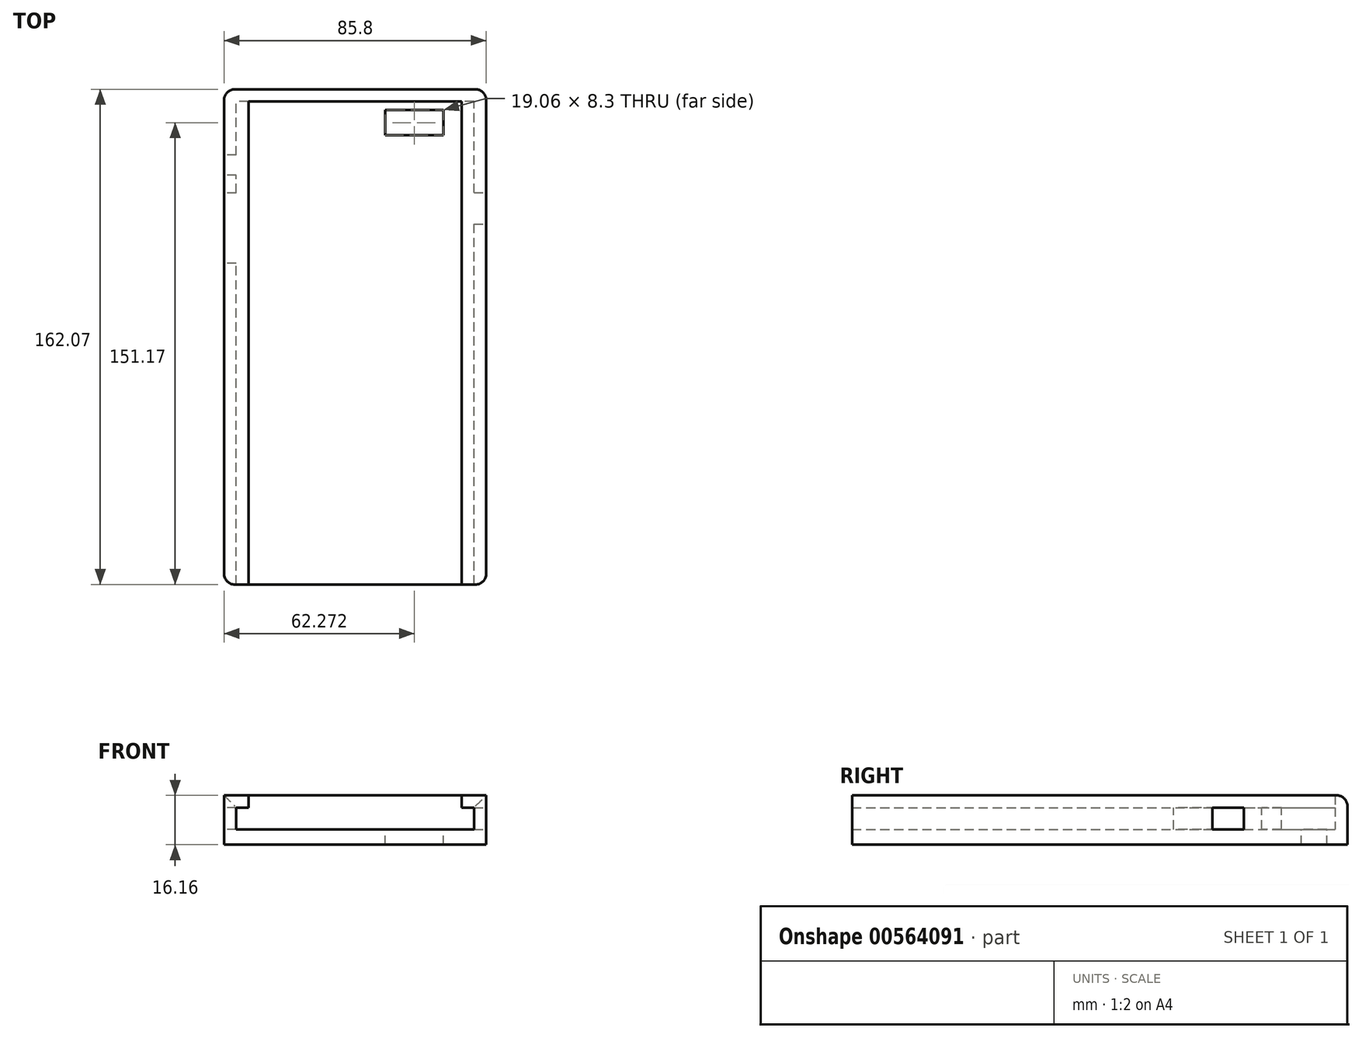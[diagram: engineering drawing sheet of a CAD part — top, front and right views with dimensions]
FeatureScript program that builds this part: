
annotation { "Feature Type Name" : "Feature", "Feature Type Description" : "" }
export const myFeature = defineFeature(function(context is Context, id is Id, definition is map)
    precondition{}
    {
        {
            var Q0;
            Q0=qCreatedBy(makeId("Front.planeOp"),FACE);
            var sketch = newSketch(context, id + "F0", { "sketchPlane" : qUnion([Q0])});
            skLineSegment(sketch, "E0", {"start": v(-41.48, -12.16) * mm, "end": v(44.32, -12.16) * mm});
            skLineSegment(sketch, "E1", {"start": v(44.32, -12.16) * mm, "end": v(44.32, 4) * mm});
            skLineSegment(sketch, "E2", {"start": v(44.32, 4) * mm, "end": v(36.32, 4) * mm});
            skLineSegment(sketch, "E3", {"start": v(36.32, 4) * mm, "end": v(36.32, 0) * mm});
            skLineSegment(sketch, "E4", {"start": v(36.32, 0) * mm, "end": v(40.32, 0) * mm});
            skLineSegment(sketch, "E5", {"start": v(40.32, 0) * mm, "end": v(40.32, -7.1) * mm});
            skLineSegment(sketch, "E6", {"start": v(40.32, -7.1) * mm, "end": v(-37.48, -7.1) * mm});
            skLineSegment(sketch, "E7", {"start": v(-37.48, -7.1) * mm, "end": v(-37.48, 0) * mm});
            skLineSegment(sketch, "E8", {"start": v(-37.48, 0) * mm, "end": v(-33.48, 0) * mm});
            skLineSegment(sketch, "E9", {"start": v(-33.48, 0) * mm, "end": v(-33.48, 4) * mm});
            skLineSegment(sketch, "E10", {"start": v(-33.48, 4) * mm, "end": v(-41.48, 4) * mm});
            skLineSegment(sketch, "E11", {"start": v(-41.48, 4) * mm, "end": v(-41.48, -12.16) * mm});
            skSolve(sketch);
        }
        {
            var Q0;
            Q0 = qSketchRegion(id + "F0", true);
            extrude(context, id + "F1", {"entities" : qUnion([Q0]), "depth" : 158.07 * mm, "offsetDistance" : 25.4 * mm});
        }
        {
            var Q0;
            Q0=makeQuery(id+"F1.opExtrude","CAP_FACE",FACE,{"disambiguationData":[OSD([sQuery(id+"F0.wireOp",EDGE,"E0"),sQuery(id+"F0.wireOp",EDGE,"E1"),sQuery(id+"F0.wireOp",EDGE,"E2"),sQuery(id+"F0.wireOp",EDGE,"E3"),sQuery(id+"F0.wireOp",EDGE,"E4"),sQuery(id+"F0.wireOp",EDGE,"E5"),sQuery(id+"F0.wireOp",EDGE,"E6"),sQuery(id+"F0.wireOp",EDGE,"E7"),sQuery(id+"F0.wireOp",EDGE,"E8"),sQuery(id+"F0.wireOp",EDGE,"E9"),sQuery(id+"F0.wireOp",EDGE,"E10"),sQuery(id+"F0.wireOp",EDGE,"E11")])],"isStart":false});
            var sketch = newSketch(context, id + "F2", { "sketchPlane" : qUnion([Q0])});
            skLineSegment(sketch, "E12.bottom", {"start": v(-41.48, 4) * mm, "end": v(44.32, 4) * mm});
            skLineSegment(sketch, "E12.top", {"start": v(-41.48, -12.16) * mm, "end": v(44.32, -12.16) * mm});
            skLineSegment(sketch, "E12.left", {"start": v(-41.48, 4) * mm, "end": v(-41.48, -12.16) * mm});
            skLineSegment(sketch, "E12.right", {"start": v(44.32, 4) * mm, "end": v(44.32, -12.16) * mm});
            skSolve(sketch);
        }
        {
            var Q0;
            Q0=qCreatedBy(makeId("Front.planeOp"),FACE);
            var sketch = newSketch(context, id + "F3", { "sketchPlane" : qUnion([Q0])});
            skLineSegment(sketch, "E13.bottom", {"start": v(44.32, 4) * mm, "end": v(-41.48, 4) * mm});
            skLineSegment(sketch, "E13.top", {"start": v(44.32, -12.16) * mm, "end": v(-41.48, -12.16) * mm});
            skLineSegment(sketch, "E13.left", {"start": v(44.32, 4) * mm, "end": v(44.32, -12.16) * mm});
            skLineSegment(sketch, "E13.right", {"start": v(-41.48, 4) * mm, "end": v(-41.48, -12.16) * mm});
            skSolve(sketch);
        }
        {
            var Q0;
            Q0 = qSketchRegion(id + "F3", true);
            extrude(context, id + "F4", {"entities" : qUnion([Q0]), "operationType" : NewBodyOperationType.ADD, "oppositeDirection" : true, "depth" : 4 * mm, "offsetDistance" : 25.4 * mm});
        }
        {
            var Q0;
            Q0=makeQuery(id+"F4.opExtrude","CAP_EDGE",EDGE,{"disambiguationData":[OSD([sQuery(id+"F3.wireOp",EDGE,"E13.right")])],"isStart":false});
            var Q1;
            Q1=makeQuery(id+"F4.opExtrude","CAP_EDGE",EDGE,{"disambiguationData":[OSD([sQuery(id+"F3.wireOp",EDGE,"E13.left")])],"isStart":false});
            var Q2;
            Q2=makeQuery(id+"F4.opExtrude","CAP_EDGE",EDGE,{"disambiguationData":[OSD([sQuery(id+"F3.wireOp",EDGE,"E13.bottom")])],"isStart":false});
            var Q3;
            Q3=makeQuery(id+"F1.opExtrude","CAP_EDGE",EDGE,{"disambiguationData":[OSD([sQuery(id+"F0.wireOp",EDGE,"E1")])],"isStart":false});
            var Q4;
            Q4=makeQuery(id+"F1.opExtrude","CAP_EDGE",EDGE,{"disambiguationData":[OSD([sQuery(id+"F0.wireOp",EDGE,"E11")])],"isStart":false});
            fillet(context, id + "F5", {"entities" : qUnion([Q0, Q1, Q2, Q3, Q4]), "radius" : 3.55 * mm, "tangentPropagation" : true, "allowEdgeOverflow" : false});
        }
        {
            var Q0;
            Q0=makeQuery(id+"F1.opExtrude","SWEPT_FACE",FACE,{"disambiguationData":[OSD([sQuery(id+"F0.wireOp",EDGE,"E6")])]});
            var sketch = newSketch(context, id + "F6", { "sketchPlane" : qUnion([Q0])});
            skLineSegment(sketch, "E14.bottom", {"start": v(11.26, -2.75) * mm, "end": v(30.32, -2.75) * mm});
            skLineSegment(sketch, "E14.top", {"start": v(11.26, -11.05) * mm, "end": v(30.32, -11.05) * mm});
            skLineSegment(sketch, "E14.left", {"start": v(11.26, -2.75) * mm, "end": v(11.26, -11.05) * mm});
            skLineSegment(sketch, "E14.right", {"start": v(30.32, -2.75) * mm, "end": v(30.32, -11.05) * mm});
            skSolve(sketch);
        }
        {
            var Q0;
            Q0=makeQuery(id+"F6.imprint","IMPRINT",FACE,{"disambiguationData":[TD([[makeQuery(id+"F6.imprint","IMPRINT",EDGE,{"derivedFrom":sQuery(id+"F6.wireOp",EDGE,"E14.bottom")}),-1.0]])]});
            extrude(context, id + "F7", {"entities" : qUnion([Q0]), "operationType" : NewBodyOperationType.REMOVE, "oppositeDirection" : true, "depth" : 10 * mm, "offsetDistance" : 25.4 * mm});
        }
        {
            var Q0;
            Q0=makeQuery(id+"F4.boolean.opBoolean","MERGE",FACE,{"derivedFrom":[makeQuery(id+"F1.opExtrude","SWEPT_FACE",FACE,{"disambiguationData":[OSD([sQuery(id+"F0.wireOp",EDGE,"E11")])]}),makeQuery(id+"F4.opExtrude","SWEPT_FACE",FACE,{"disambiguationData":[OSD([sQuery(id+"F3.wireOp",EDGE,"E13.right")])]})]});
            var sketch = newSketch(context, id + "F8", { "sketchPlane" : qUnion([Q0])});
            skLineSegment(sketch, "E15.bottom", {"start": v(17.55, -7.1) * mm, "end": v(24.05, -7.1) * mm});
            skLineSegment(sketch, "E15.top", {"start": v(17.55, 0) * mm, "end": v(24.05, 0) * mm});
            skLineSegment(sketch, "E15.left", {"start": v(17.55, -7.1) * mm, "end": v(17.55, 0) * mm});
            skLineSegment(sketch, "E15.right", {"start": v(24.05, -7.1) * mm, "end": v(24.05, 0) * mm});
            skLineSegment(sketch, "E16.bottom", {"start": v(29.93, -7.1) * mm, "end": v(52.93, -7.1) * mm});
            skLineSegment(sketch, "E16.top", {"start": v(29.93, 0) * mm, "end": v(52.93, 0) * mm});
            skLineSegment(sketch, "E16.left", {"start": v(29.93, -7.1) * mm, "end": v(29.93, 0) * mm});
            skLineSegment(sketch, "E16.right", {"start": v(52.93, -7.1) * mm, "end": v(52.93, 0) * mm});
            skSolve(sketch);
        }
        {
            var Q0;
            Q0 = qSketchRegion(id + "F8", true);
            extrude(context, id + "F9", {"entities" : qUnion([Q0]), "operationType" : NewBodyOperationType.REMOVE, "oppositeDirection" : true, "depth" : 4 * mm, "offsetDistance" : 25.4 * mm});
        }
        {
            var Q0;
            Q0=makeQuery(id+"F4.boolean.opBoolean","MERGE",FACE,{"derivedFrom":[makeQuery(id+"F1.opExtrude","SWEPT_FACE",FACE,{"disambiguationData":[OSD([sQuery(id+"F0.wireOp",EDGE,"E1")])]}),makeQuery(id+"F4.opExtrude","SWEPT_FACE",FACE,{"disambiguationData":[OSD([sQuery(id+"F3.wireOp",EDGE,"E13.left")])]})]});
            var sketch = newSketch(context, id + "F10", { "sketchPlane" : qUnion([Q0])});
            skLineSegment(sketch, "E17.bottom", {"start": v(-40.15, 0) * mm, "end": v(-29.85, 0) * mm});
            skLineSegment(sketch, "E17.top", {"start": v(-40.15, -7.1) * mm, "end": v(-29.85, -7.1) * mm});
            skLineSegment(sketch, "E17.left", {"start": v(-40.15, 0) * mm, "end": v(-40.15, -7.1) * mm});
            skLineSegment(sketch, "E17.right", {"start": v(-29.85, 0) * mm, "end": v(-29.85, -7.1) * mm});
            skSolve(sketch);
        }
        {
            var Q0;
            Q0=makeQuery(id+"F10.imprint","IMPRINT",FACE,{"disambiguationData":[TD([[makeQuery(id+"F10.imprint","IMPRINT",EDGE,{"derivedFrom":sQuery(id+"F10.wireOp",EDGE,"E17.bottom")}),-1.0]])]});
            extrude(context, id + "F11", {"entities" : qUnion([Q0]), "operationType" : NewBodyOperationType.REMOVE, "oppositeDirection" : true, "depth" : 4 * mm, "offsetDistance" : 25.4 * mm});
        }
    });
